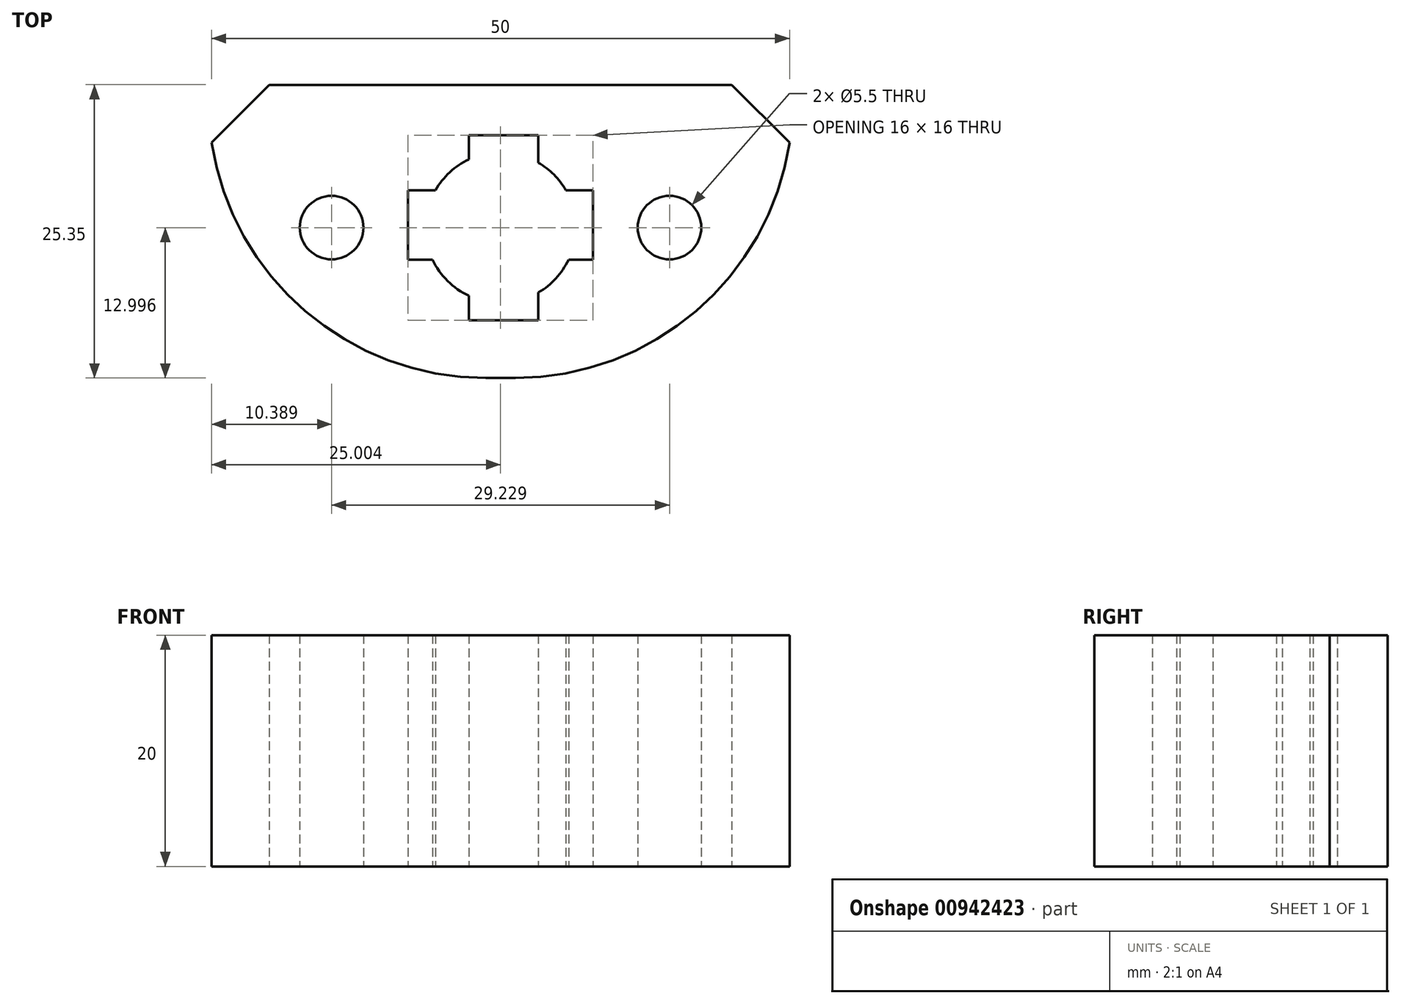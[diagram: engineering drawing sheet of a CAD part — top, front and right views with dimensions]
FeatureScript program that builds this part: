
annotation { "Feature Type Name" : "Feature", "Feature Type Description" : "" }
export const myFeature = defineFeature(function(context is Context, id is Id, definition is map)
    precondition{}
    {
        {
            var Q0;
            Q0=qCreatedBy(makeId("Top.planeOp"),FACE);
            var sketch = newSketch(context, id + "F0", { "sketchPlane" : qUnion([Q0])});
            skLineSegment(sketch, "E0.0.0", {"start": v(20.05, 11.18) * mm, "end": v(25.05, 6.18) * mm});
            skArc(sketch, "E0.0.1", {"start": v(25.05, 6.18) * mm, "mid": v(16.96, -8.39) * mm, "end": v(1.33, -14.17) * mm});
            skLineSegment(sketch, "E0.0.2", {"start": v(1.33, -14.17) * mm, "end": v(-1.22, -14.17) * mm});
            skArc(sketch, "E0.0.3", {"start": v(-1.22, -14.17) * mm, "mid": v(-16.85, -8.39) * mm, "end": v(-24.95, 6.18) * mm});
            skLineSegment(sketch, "E0.0.4", {"start": v(-24.95, 6.18) * mm, "end": v(-19.95, 11.18) * mm});
            skLineSegment(sketch, "E0.0.5", {"start": v(-19.95, 11.18) * mm, "end": v(20.05, 11.18) * mm});
            skCircle(sketch, "E1.0", {"center": v(-14.56, -1.17) * mm, "radius": 2.75 * mm});
            skCircle(sketch, "E2.0", {"center": v(14.67, -1.17) * mm, "radius": 2.75 * mm});
            skLineSegment(sketch, "E3.0", {"start": v(8.05, 2.06) * mm, "end": v(8.05, -3.94) * mm});
            skArc(sketch, "E4.0", {"start": v(3.33, -6.79) * mm, "mid": v(4.85, -5.56) * mm, "end": v(5.93, -3.94) * mm});
            skArc(sketch, "E5.0", {"start": v(-2.67, 4.73) * mm, "mid": v(-4.34, 3.62) * mm, "end": v(-5.59, 2.06) * mm});
            skLineSegment(sketch, "E6.0", {"start": v(-7.95, -3.94) * mm, "end": v(-7.95, 2.06) * mm});
            skArc(sketch, "E7.0", {"start": v(-5.83, -3.94) * mm, "mid": v(-4.53, -5.79) * mm, "end": v(-2.67, -7.07) * mm});
            skLineSegment(sketch, "E8.0", {"start": v(-2.67, 6.83) * mm, "end": v(3.33, 6.83) * mm});
            skLineSegment(sketch, "E9.0", {"start": v(3.33, -6.79) * mm, "end": v(3.33, -9.17) * mm});
            skLineSegment(sketch, "E10.0", {"start": v(8.05, -3.94) * mm, "end": v(5.93, -3.94) * mm});
            skLineSegment(sketch, "E11.0", {"start": v(5.7, 2.06) * mm, "end": v(8.05, 2.06) * mm});
            skLineSegment(sketch, "E12.0", {"start": v(-2.67, -9.17) * mm, "end": v(-2.67, -7.07) * mm});
            skLineSegment(sketch, "E13.0", {"start": v(3.33, -9.17) * mm, "end": v(-2.67, -9.17) * mm});
            skLineSegment(sketch, "E14.0", {"start": v(-7.95, 2.06) * mm, "end": v(-5.59, 2.06) * mm});
            skLineSegment(sketch, "E15.0", {"start": v(-5.83, -3.94) * mm, "end": v(-7.95, -3.94) * mm});
            skLineSegment(sketch, "E16.0", {"start": v(-2.67, 4.73) * mm, "end": v(-2.67, 6.83) * mm});
            skLineSegment(sketch, "E17.0", {"start": v(3.33, 6.83) * mm, "end": v(3.33, 4.44) * mm});
            skArc(sketch, "E18.0", {"start": v(5.7, 2.06) * mm, "mid": v(4.67, 3.4) * mm, "end": v(3.33, 4.44) * mm});
            skSolve(sketch);
        }
        {
            var Q0;
            Q0 = qSketchRegion(id + "F0", true);
            var Q1;
            Q1=makeQuery(id+"F0.imprint","IMPRINT",FACE,{"disambiguationData":[TD([[makeQuery(id+"F0.imprint","IMPRINT",EDGE,{"derivedFrom":sQuery(id+"F0.wireOp",EDGE,"E0.0.0")}),-1.0]])]});
            extrude(context, id + "F1", {"entities" : qUnion([Q0, Q1]), "depth" : 20 * mm, "offsetDistance" : 25 * mm});
        }
    });
